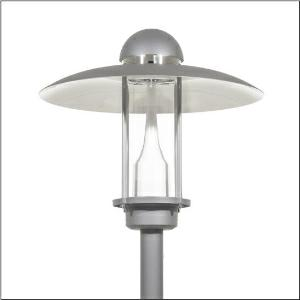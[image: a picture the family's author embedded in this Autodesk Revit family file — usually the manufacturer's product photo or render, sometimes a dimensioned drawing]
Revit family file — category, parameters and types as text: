
# Revit family: city-light_elegance_iq___st1_2a_5xa5265mf14h_1b27
name_source: partatom
category: Lighting Fixtures
units: mm (PartAtom-declared; Revit-internal decimal feet)

## family parameters
Cut with Voids When Loaded = No
Host = Face
Light Source = No
Part Type = Normal
Room Calculation Point = No
Round Connector Dimension = Use Diameter
Shared = No

## types (1)
- --- (1 x LED, 1470 lm, 11.8 W, 2700K)
    Apparent Load = 12 VA
    CIE Flux Codes = 22 62 94 98 100
    Color Rendering = 70
    Color Temperature = 2700K
    Default Elevation = 1800 mm
    Description = City-Light Elegance iQ, mast luminaire, Module 540 iQ-SR, primary light control with 3 zone facetted reflector, of plastic, silver coated, highly specular, structured, primary optical cover: cover, of PMMA, transparent, light distribution: ST1.2a, light emission: direct distribution, primary light characteristic: asymmetric, installation type: post-top, LED, High Power LED, rated luminous flux: 1.470lm, luminous efficacy: 124lm/W, light colour: 727, colour temperature: 2700K, control gear: ECG iQ, control: presetting dimming logarithmic, Street-Remote, Auto-Match, Temp-Guard, Lumen-Switch, Night-Set, Smart-Wire, Light-Fading, Desk-Remote (wireless, voltage-free reading and setting of iQ features in the workshop via application-optimized NFC function/RFID function), optimised constant luminous flux control (CLO 2.0), with terminal, 6-pole, max. 2.5mm², mains connection: 230..240V, AC, 50/60Hz, start of lifetime: 12W, end of service life: 12W, reduction: 6W, luminaire housing, upper part, of aluminium, coated, Siteco® metallic grey (DB 702S), diameter: 750mm, height: 675mm, spigot size: d x l = 76 x 70mm (post-top) | with reducer (optional accessory) 60 x 70mm, post-top mast mounting element, of diecast aluminium, coated, Siteco® metallic grey (DB 702S), Module 540 iQ-SR, traffic white (RAL 9016), equipment: standard, protection rating (complete): IP65, insulation class (complete): insulation class II (safety insulation), certification: CE, ENEC, VDE, packaging unit: 1 piece

Light Distribution: ST1.2a
    Height = 675 mm
    Lamp = 1 x LED
    Lamp Light Flux = 1470 lm
    Lamp Power = 11.8 W
    Lamp count = 1
    Length = 750 mm
    Luminous efficacy = 125 lm/W
    Manufacturer = Siteco
    ModVariant = No
    Model = 5XA5265MF14H
    Number of Poles = 1
    OnlyDefault = Yes
    Power Factor = 1
    Product Name = City-Light Elegance iQ | ST1.2a
    Product group = mast luminaire | pylon top
    ProductGroupID = 6100
    Protection Class = Protection class II
    Protection Degree = IP 65
    RLX_Detail_Level = 1
    RLX_Emergency_Light_Flux = 0 lm
    RLX_Emergency_Type = 0
    RLX_Emergency_Type_DB = No
    RlxData = <blob elided: 99577 chars, md5=a643da66>
    Socket = socket
    Standby Power = 0 W
    System Light Flux = 1470 lm
    System Power = 12 W
    Type Comments = factory setting: luminous flux: 100 % | dim-lin: 254 | 472 mA
    Type Image = l_1006912.jpg
    URL = http://relux.com
    VarID = @adj_085551
    Voltage = 0 V
    Weight = 0.00 kg
    Width = 0 mm  [stored 0 ft]

note: [stored X ft] marks values corroborated as IEEE doubles in the binary element streams (Revit-internal decimal feet)

## geometry (parser evidence)
native form markers: Blend x4, Sweep x11
no freeform markers — native parametric forms only
